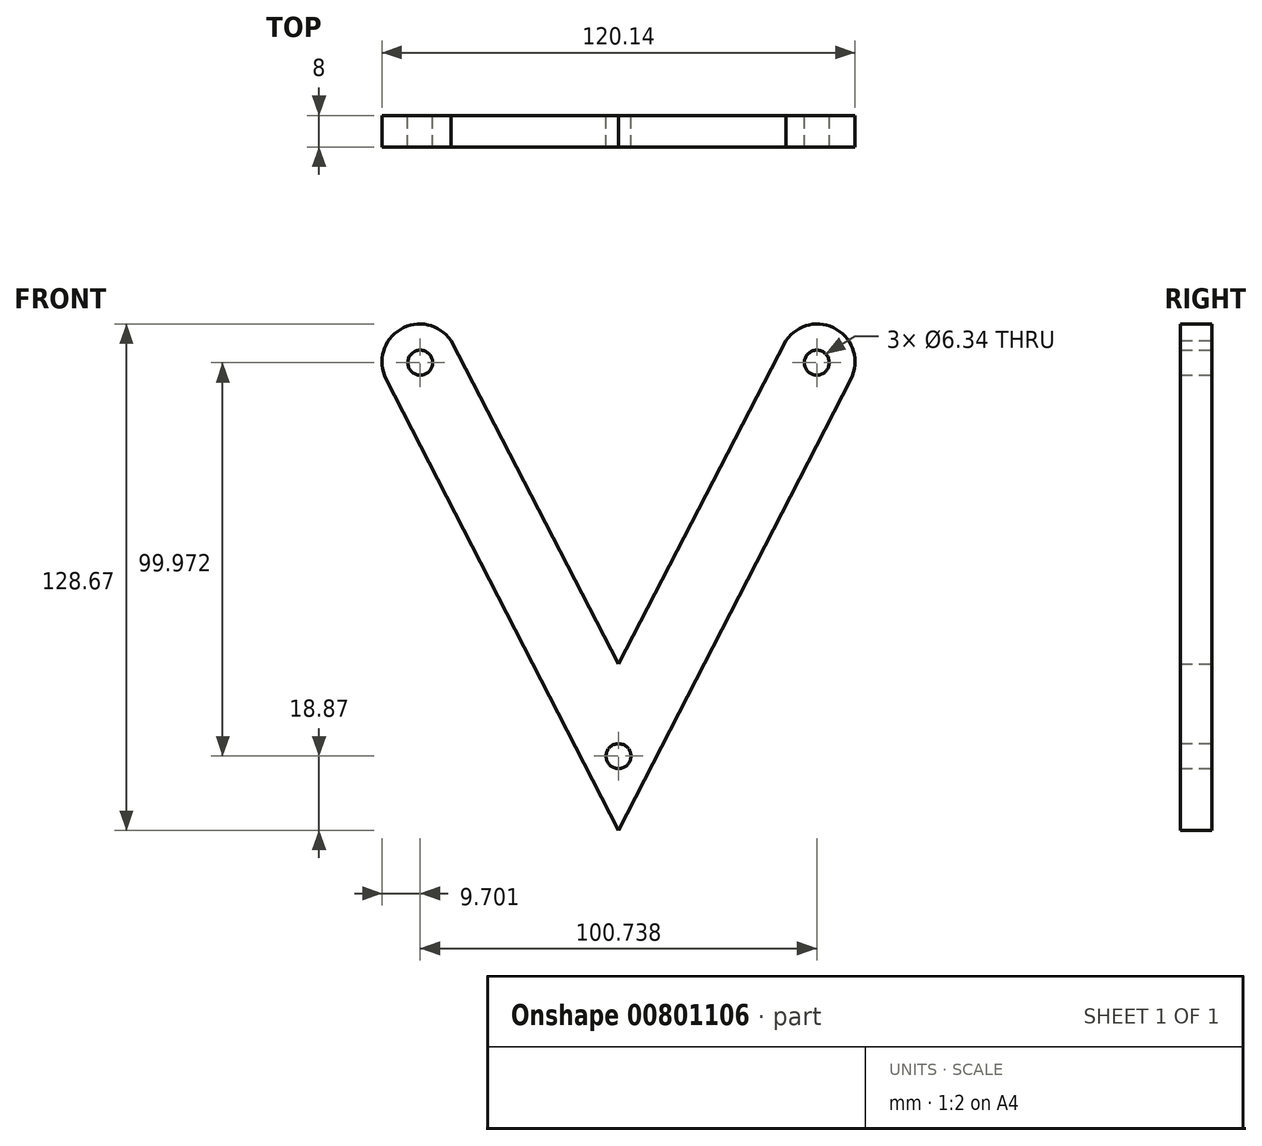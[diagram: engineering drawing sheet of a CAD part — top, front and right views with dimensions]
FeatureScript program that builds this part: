
annotation { "Feature Type Name" : "Feature", "Feature Type Description" : "" }
export const myFeature = defineFeature(function(context is Context, id is Id, definition is map)
    precondition{}
    {
        {
            var Q0;
            Q0=qCreatedBy(makeId("Front.planeOp"),FACE);
            var sketch = newSketch(context, id + "F0", { "sketchPlane" : qUnion([Q0])});
            skCircle(sketch, "E0", {"center": v(0, 0) * mm, "radius": 3.17 * mm});
            skSolve(sketch);
        }
        {
            var Q0;
            Q0=qCreatedBy(makeId("Front.planeOp"),FACE);
            var sketch = newSketch(context, id + "F1", { "sketchPlane" : qUnion([Q0])});
            skLineSegment(sketch, "E1", {"start": v(0, 0) * mm, "end": v(0, 99.98) * mm});
            skLineSegment(sketch, "E2", {"start": v(0, 0) * mm, "end": v(-50.38, 0) * mm});
            skLineSegment(sketch, "E3", {"start": v(-50.38, 0) * mm, "end": v(-50.38, 99.98) * mm});
            skLineSegment(sketch, "E4.MirrorCS", {"start": v(0, 0) * mm, "end": v(50.38, 0) * mm});
            skLineSegment(sketch, "E5.MirrorCS", {"start": v(50.38, 0) * mm, "end": v(50.38, 99.98) * mm});
            skSolve(sketch);
        }
        {
            var Q0;
            Q0=qCreatedBy(makeId("Front.planeOp"),FACE);
            var sketch = newSketch(context, id + "F2", { "sketchPlane" : qUnion([Q0])});
            skCircle(sketch, "E6", {"center": v(-50.37, 99.97) * mm, "radius": 3.17 * mm});
            skCircle(sketch, "E7.MirrorC", {"center": v(50.37, 99.97) * mm, "radius": 3.17 * mm});
            skSolve(sketch);
        }
        {
            var Q0;
            Q0=qCreatedBy(makeId("Front.planeOp"),FACE);
            var sketch = newSketch(context, id + "F3", { "sketchPlane" : qUnion([Q0])});
            skLineSegment(sketch, "E8", {"start": v(0, -18.87) * mm, "end": v(-59, 95.84) * mm});
            skArc(sketch, "E9", {"start": v(-42.58, 105.63) * mm, "mid": v(-55.4, 108.45) * mm, "end": v(-59, 95.84) * mm});
            skLineSegment(sketch, "E10", {"start": v(-42.58, 105.63) * mm, "end": v(0, 23.47) * mm});
            skLineSegment(sketch, "E11.MirrorCS", {"start": v(42.58, 105.63) * mm, "end": v(0, 23.47) * mm});
            skLineSegment(sketch, "E12.MirrorCS", {"start": v(0, -18.87) * mm, "end": v(59, 95.84) * mm});
            skArc(sketch, "E13.MirrorCS", {"start": v(42.58, 105.63) * mm, "mid": v(55.4, 108.45) * mm, "end": v(59, 95.84) * mm});
            skSolve(sketch);
        }
        {
            var Q0;
            Q0 = qSketchRegion(id + "F3", true);
            extrude(context, id + "F4", {"entities" : qUnion([Q0]), "depth" : 8 * mm, "offsetDistance" : 25 * mm});
        }
        {
            var Q0;
            Q0 = qSketchRegion(id + "F2", true);
            extrude(context, id + "F5", {"entities" : qUnion([Q0]), "operationType" : NewBodyOperationType.REMOVE, "depth" : 25 * mm, "offsetDistance" : 25 * mm});
        }
        {
            var Q0;
            Q0 = qSketchRegion(id + "F0", true);
            extrude(context, id + "F6", {"entities" : qUnion([Q0]), "operationType" : NewBodyOperationType.REMOVE, "depth" : 25 * mm, "offsetDistance" : 25 * mm});
        }
    });
